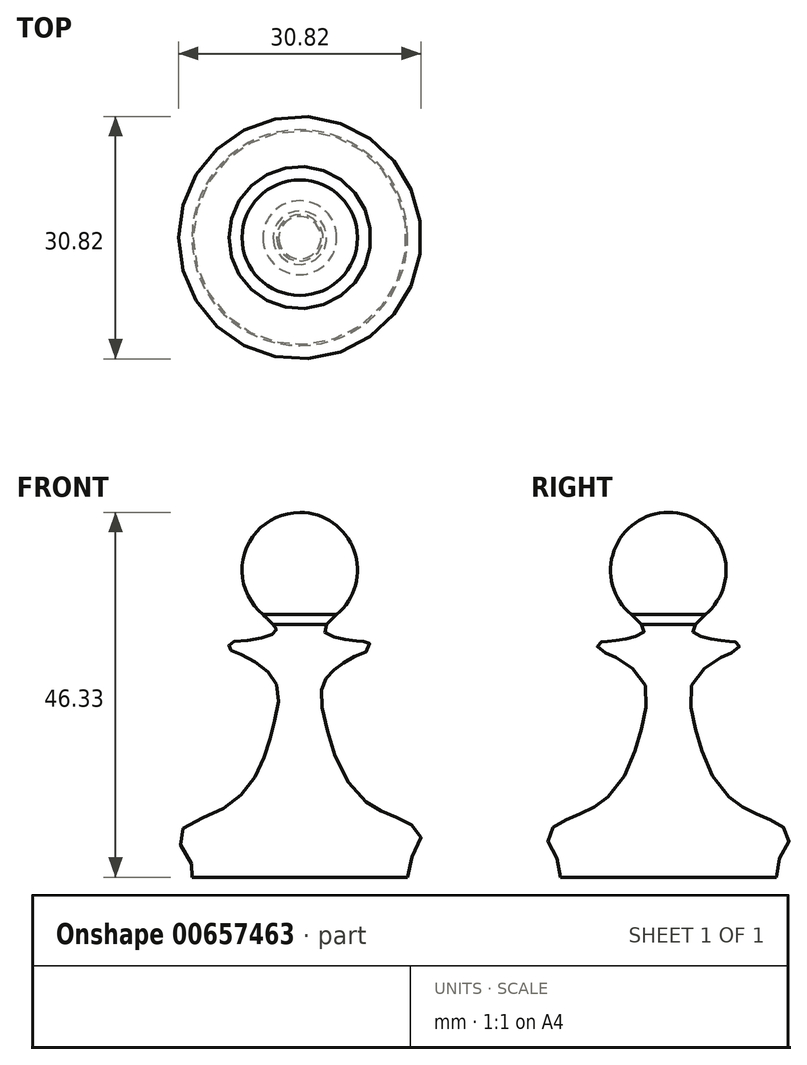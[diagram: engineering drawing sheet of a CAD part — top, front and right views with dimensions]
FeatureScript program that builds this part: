
annotation { "Feature Type Name" : "Feature", "Feature Type Description" : "" }
export const myFeature = defineFeature(function(context is Context, id is Id, definition is map)
    precondition{}
    {
        {
            var Q0;
            Q0=qCreatedBy(makeId("Front.planeOp"),FACE);
            var sketch = newSketch(context, id + "F0", { "sketchPlane" : qUnion([Q0])});
            skSolve(sketch);
        }
        {
            var Q0;
            Q0=qCreatedBy(makeId("Front.planeOp"),FACE);
            var sketch = newSketch(context, id + "F1", { "sketchPlane" : qUnion([Q0])});
            skArc(sketch, "E0", {"start": v(0, 46.33) * mm, "mid": v(-6.9, 41.5) * mm, "end": v(-4.7, 33.36) * mm});
            skPoint(sketch, "E1.start.orphan", {"position": v(-13.7, 0) * mm});
            skFitSpline(sketch, "E2", {"points": [v(-13.7, 0) * mm, v(-13.7, 1.55) * mm, v(-15.4, 5.16) * mm, v(-12.58, 7.44) * mm, v(-8.38, 9.58) * mm, v(-5.39, 13.28) * mm, v(-3.96, 16.9) * mm, v(-3.14, 20.08) * mm, v(-2.7, 23.45) * mm, v(-3.52, 25.44) * mm, v(-5.33, 27.08) * mm, v(-7.43, 28.24) * mm, v(-8.58, 28.7) * mm, v(-8.9, 28.92) * mm, v(-9.02, 29.25) * mm, v(-8.94, 29.6) * mm, v(-8.6, 29.88) * mm, v(-8.16, 29.94) * mm, v(-6.02, 30.18) * mm, v(-4.45, 30.47) * mm, v(-3.54, 30.83) * mm, v(-3.16, 31.1) * mm, v(-2.96, 31.46) * mm, v(-3.08, 31.83) * mm, v(-3.41, 32.13) * mm], "startDerivative": vector(9.22, 33.32) * mm, "endDerivative": vector(-16.64, 12.4) * mm});
            skFitSpline(sketch, "E3", {"points": [v(-3.41, 32.13) * mm, v(-4.7, 33.36) * mm], "startDerivative": vector(-1.28, 1.24) * mm, "endDerivative": vector(-1.28, 1.24) * mm});
            skLineSegment(sketch, "E4", {"start": v(0, -6.4) * mm, "end": v(0, 52.75) * mm, "construction": true});
            skLineSegment(sketch, "E5", {"start": v(-13.7, 0) * mm, "end": v(0, 0) * mm});
            skLineSegment(sketch, "E6", {"start": v(0, 0) * mm, "end": v(0, 46.33) * mm});
            skSolve(sketch);
        }
        {
            var Q0;
            Q0=makeQuery(id+"F1.imprint","IMPRINT",FACE,{"disambiguationData":[TD([[makeQuery(id+"F1.imprint","IMPRINT",EDGE,{"derivedFrom":sQuery(id+"F1.wireOp",EDGE,"E0")}),1.0]])]});
            var Q1;
            Q1=sQuery(id+"F1.wireOp",EDGE,"E4");
            revolve(context, id + "F2", {"entities" : qUnion([Q0]), "axis" : qUnion([Q1]), "revolveType" : RevolveType.FULL});
        }
    });
